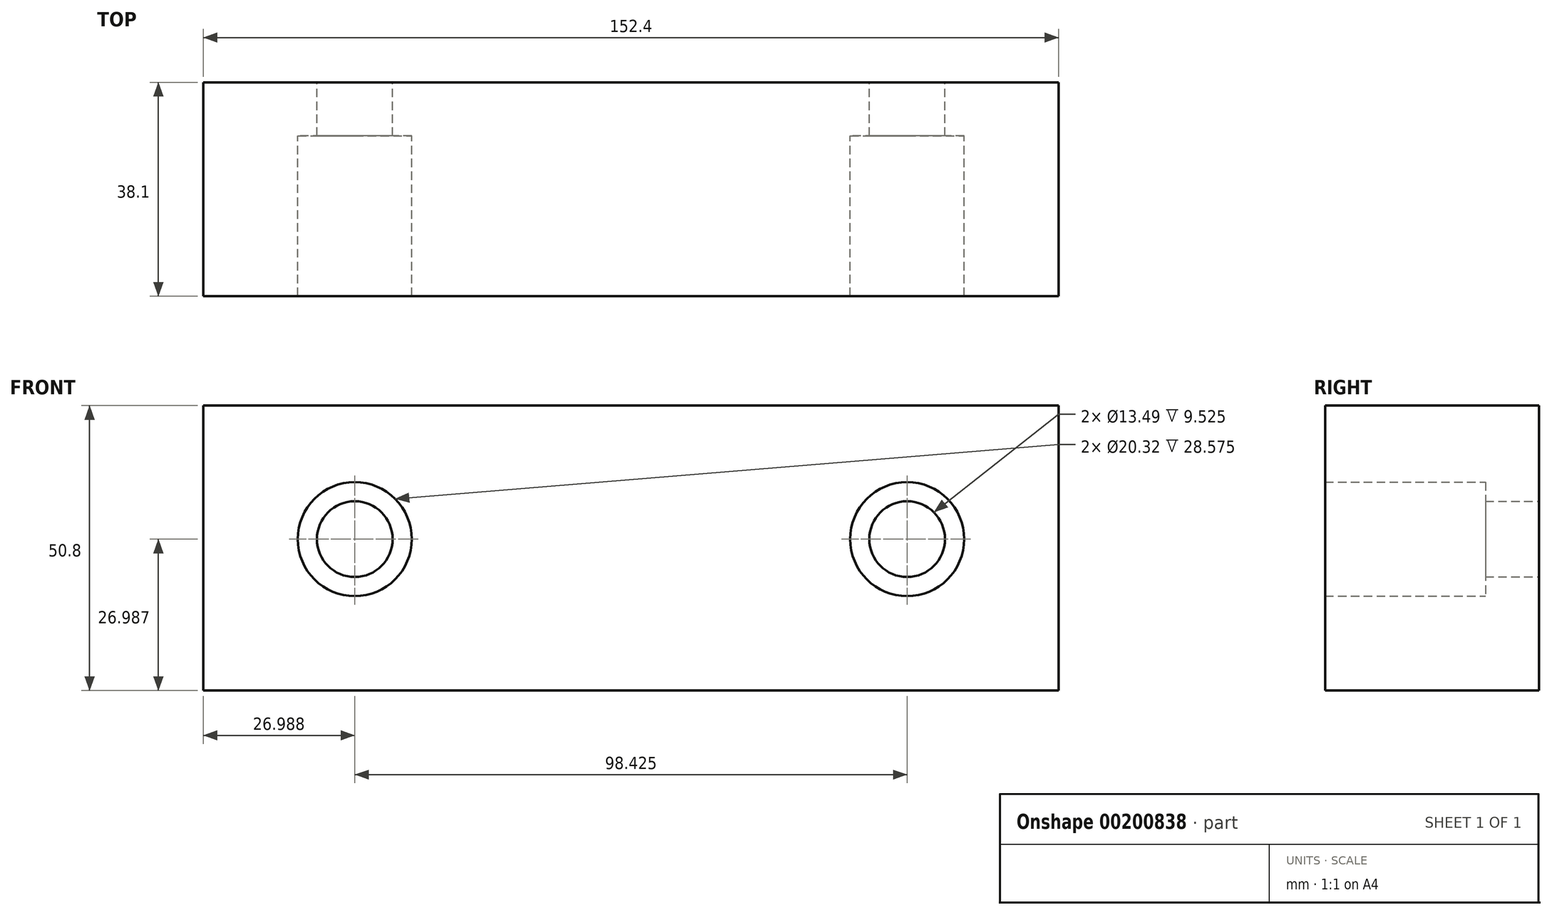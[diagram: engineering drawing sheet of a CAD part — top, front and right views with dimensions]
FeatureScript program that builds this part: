
annotation { "Feature Type Name" : "Feature", "Feature Type Description" : "" }
export const myFeature = defineFeature(function(context is Context, id is Id, definition is map)
    precondition{}
    {
        {
            var Q0;
            Q0=qCreatedBy(makeId("Front.planeOp"),FACE);
            var sketch = newSketch(context, id + "F0", { "sketchPlane" : qUnion([Q0])});
            skLineSegment(sketch, "E0.bottom", {"start": v(-76.2, 0) * mm, "end": v(76.2, 0) * mm});
            skLineSegment(sketch, "E0.top", {"start": v(-76.2, -50.8) * mm, "end": v(76.2, -50.8) * mm});
            skLineSegment(sketch, "E0.left", {"start": v(-76.2, 0) * mm, "end": v(-76.2, -50.8) * mm});
            skLineSegment(sketch, "E0.right", {"start": v(76.2, 0) * mm, "end": v(76.2, -50.8) * mm});
            skSolve(sketch);
        }
        {
            var Q0;
            Q0 = qSketchRegion(id + "F0", true);
            extrude(context, id + "F1", {"entities" : qUnion([Q0]), "depth" : 38.1 * mm});
        }
        {
            var Q0;
            Q0=makeQuery(id+"F1.opExtrude","CAP_FACE",FACE,{"disambiguationData":[OSD([sQuery(id+"F0.wireOp",EDGE,"E0.bottom"),sQuery(id+"F0.wireOp",EDGE,"E0.top"),sQuery(id+"F0.wireOp",EDGE,"E0.left"),sQuery(id+"F0.wireOp",EDGE,"E0.right")])],"isStart":true});
            var sketch = newSketch(context, id + "F2", { "sketchPlane" : qUnion([Q0])});
            skCircle(sketch, "E1", {"center": v(49.21, -23.81) * mm, "radius": 6.74 * mm});
            skCircle(sketch, "E2", {"center": v(-49.21, -23.81) * mm, "radius": 6.74 * mm});
            skSolve(sketch);
        }
        {
            var Q0;
            Q0 = qSketchRegion(id + "F2", true);
            extrude(context, id + "F3", {"entities" : qUnion([Q0]), "operationType" : NewBodyOperationType.REMOVE, "oppositeDirection" : true, "depth" : 9.52 * mm});
        }
        {
            var Q0;
            Q0=makeQuery(id+"F3.boolean.opBoolean","COPY",FACE,{"derivedFrom":makeQuery(id+"F3.opExtrude","CAP_FACE",FACE,{"disambiguationData":[OSD([sQuery(id+"F2.wireOp",EDGE,"E2")])],"isStart":false})});
            var sketch = newSketch(context, id + "F4", { "sketchPlane" : qUnion([Q0])});
            skCircle(sketch, "E3", {"center": v(-49.21, -23.81) * mm, "radius": 10.16 * mm});
            skCircle(sketch, "E4", {"center": v(49.21, -23.81) * mm, "radius": 10.16 * mm});
            skSolve(sketch);
        }
        {
            var Q0;
            Q0 = qSketchRegion(id + "F4", true);
            extrude(context, id + "F5", {"entities" : qUnion([Q0]), "operationType" : NewBodyOperationType.REMOVE, "oppositeDirection" : true, "depth" : 152.4 * mm});
        }
    });
